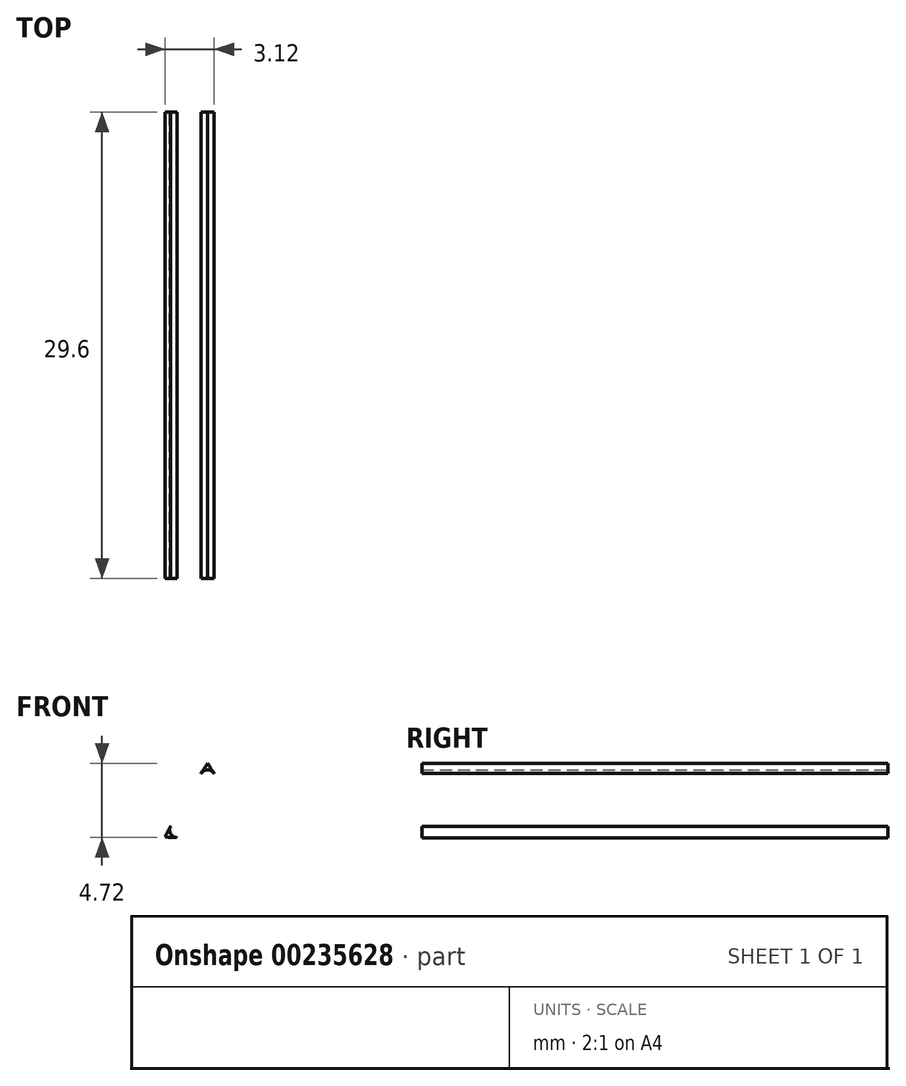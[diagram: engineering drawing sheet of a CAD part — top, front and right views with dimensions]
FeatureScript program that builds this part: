
annotation { "Feature Type Name" : "Feature", "Feature Type Description" : "" }
export const myFeature = defineFeature(function(context is Context, id is Id, definition is map)
    precondition{}
    {
        {
            var Q0;
            Q0=qCreatedBy(makeId("Front.planeOp"),FACE);
            var sketch = newSketch(context, id + "F0", { "sketchPlane" : qUnion([Q0])});
            skFitSpline(sketch, "E0", {"points": [v(0, 0) * mm, v(1.26, 2.39) * mm, v(2.7, 4.68) * mm], "startDerivative": vector(2.44, 4.83) * mm, "endDerivative": vector(2.96, 4.53) * mm});
            skFitSpline(sketch, "E1", {"points": [v(5.4, 0) * mm, v(4.14, 2.39) * mm, v(2.7, 4.68) * mm], "startDerivative": vector(-2.44, 4.83) * mm, "endDerivative": vector(-2.96, 4.53) * mm});
            skFitSpline(sketch, "E2", {"points": [v(5.4, 0) * mm, v(2.7, -0.1) * mm, v(0, 0) * mm], "startDerivative": vector(-5.4, -0.3) * mm, "endDerivative": vector(-5.4, 0.3) * mm});
            skArc(sketch, "E3.filletArc", {"start": v(0.35, 0.69) * mm, "mid": v(0.36, 0.2) * mm, "end": v(0.77, -0.04) * mm});
            skArc(sketch, "E4.filletArc", {"start": v(3.12, 4.03) * mm, "mid": v(2.7, 4.26) * mm, "end": v(2.28, 4.03) * mm});
            skArc(sketch, "E5.filletArc", {"start": v(4.63, -0.04) * mm, "mid": v(5.04, 0.2) * mm, "end": v(5.05, 0.69) * mm});
            skSolve(sketch);
        }
        {
            var Q0;
            Q0=makeQuery(id+"F0.imprint","IMPRINT",FACE,{"disambiguationData":[TD([[makeQuery(id+"F0.imprint","IMPRINT",EDGE,{"derivedFrom":sQuery(id+"F0.wireOp",EDGE,"E0")}),-1.0]])]});
            extrude(context, id + "F1", {"entities" : qUnion([Q0]), "depth" : 29.6 * mm});
        }
    });
